# Revit family: Bicycle-Racks_Huntco_Rambler5
name_source: partatom
category: Site
units: mm (PartAtom-declared; Revit-internal decimal feet)

## family parameters
Classification Number = 23.40.10.11.11
Cut with Voids When Loaded = No
Host = Face
Part Type = Normal
Round Connector Dimension = Use Diameter
Shared = No

## types (4) — shared parameters
Assembly Code = G2040500
Capacity = 5 Bikes
Construction Details = http://www.arcat.com
Covered Flange = No
Default Elevation = 4' - 0"
Description = Huntco BR Series Bike Rack - Model BR-5
Embedded Mounted = No
Exposed Flange = Yes
Flange Mounted = Yes
Freestanding = Yes
Green Building-LEED = http://www.arcat.com
Keynote = 02871
Manufacturer = Huntco Supply LLC
Manufacturer Fax = 503-274-2055
Manufacturer Website = http://www.huntco.com
Material Finish = Metal - Steel - Huntco - Stainless
Model = BR-5
Product Data = http://www.arcat.com
Revision = R1_11_2012
Send Message = http://www.arcat.com
Specification = http://www.arcat.com
URL = http://www.huntco.com
Unit Weight = 60
Unit Width = 3' - 2 3/8"
extralength = 0' - 0"
flangeheight = 0' - 0 1/2"
flangevisible = Yes
holedepth = 0' - 4"
holediameter = 0' - 0 1/2"
zero-valued in all types: Expected Lifespan (Years), Maintenance Schedule (Months), Warranty Duration (Years)

## per-type parameters (varying)
| type | Outer Radius | Pipe Diameter | Unit Height |
| 1.625D Pipe 42H | 0' - 0 13/16" | 0' - 1 5/8" | 3' - 6" |
| 1.625D Pipe 36H | 0' - 0 13/16" | 0' - 1 5/8" | 3' - 0" |
| 2.375D Pipe 42H | 0' - 1 3/16" | 0' - 2 3/8" | 3' - 6" |
| 2.375D Pipe 36H | 0' - 1 3/16" | 0' - 2 3/8" | 3' - 0" |

## geometry (parser evidence)
native form markers: Blend x4, Sweep x2
no freeform markers — native parametric forms only
